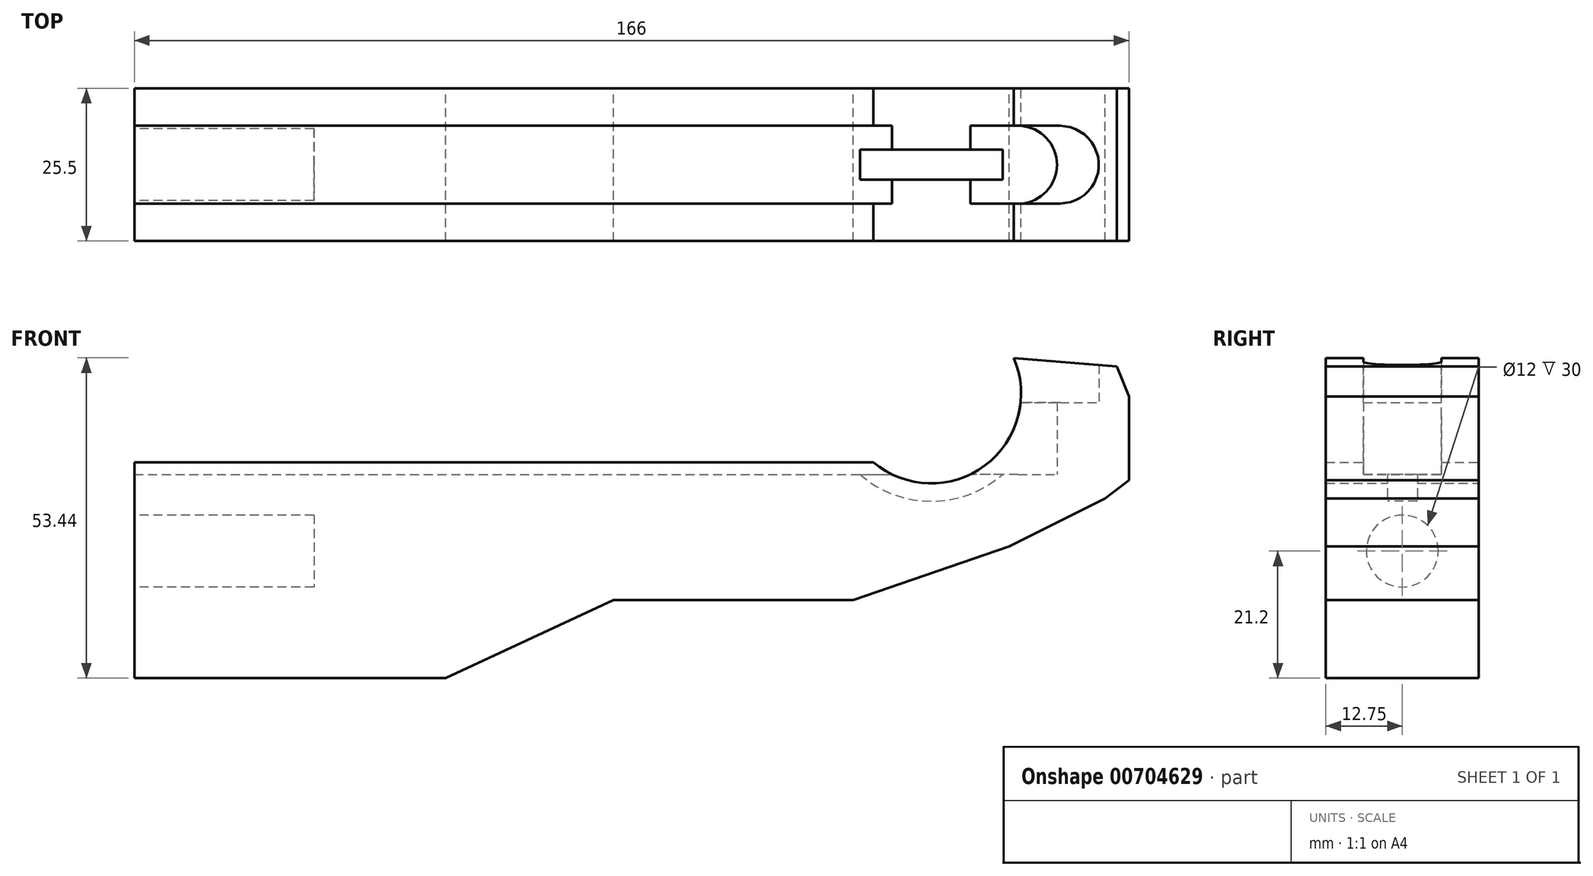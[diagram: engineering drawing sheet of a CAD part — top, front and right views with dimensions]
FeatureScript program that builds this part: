
annotation { "Feature Type Name" : "Feature", "Feature Type Description" : "" }
export const myFeature = defineFeature(function(context is Context, id is Id, definition is map)
    precondition{}
    {
        {
            var Q0;
            Q0=qCreatedBy(makeId("Front.planeOp"),FACE);
            var sketch = newSketch(context, id + "F0", { "sketchPlane" : qUnion([Q0])});
            skLineSegment(sketch, "E0", {"start": v(0, 0) * mm, "end": v(0, 36) * mm});
            skLineSegment(sketch, "E1", {"start": v(0, 36) * mm, "end": v(146, 36) * mm});
            skLineSegment(sketch, "E2", {"start": v(146, 36) * mm, "end": v(146, 53.5) * mm});
            skLineSegment(sketch, "E3", {"start": v(146, 53.5) * mm, "end": v(164, 52) * mm});
            skLineSegment(sketch, "E4", {"start": v(164, 52) * mm, "end": v(166, 47) * mm});
            skLineSegment(sketch, "E5", {"start": v(166, 47) * mm, "end": v(166, 33) * mm});
            skLineSegment(sketch, "E6", {"start": v(166, 33) * mm, "end": v(162, 30) * mm});
            skLineSegment(sketch, "E7", {"start": v(162, 30) * mm, "end": v(146, 22) * mm});
            skLineSegment(sketch, "E8", {"start": v(146, 22) * mm, "end": v(120, 13) * mm});
            skLineSegment(sketch, "E9", {"start": v(120, 13) * mm, "end": v(80, 13) * mm});
            skLineSegment(sketch, "E10", {"start": v(80, 13) * mm, "end": v(52, 0) * mm});
            skLineSegment(sketch, "E11", {"start": v(52, 0) * mm, "end": v(0, 0) * mm});
            skCircle(sketch, "E12", {"center": v(133, 47.5) * mm, "radius": 15 * mm});
            skSolve(sketch);
        }
        {
            var Q0;
            {var subQ4=sQuery(id+"F0.wireOp",EDGE,"E0");Q0=makeQuery(id+"F0.imprint","IMPRINT",FACE,{"disambiguationData":[TD([[makeQuery(id+"F0.imprint","IMPRINT",EDGE,{"derivedFrom":subQ4}),-1.0]])]});}
            var Q1;
            {var subQ0=sQuery(id+"F0.wireOp",EDGE,"E2");var subQ1=sQuery(id+"F0.wireOp",EDGE,"E1");var subQ2=makeQuery(id+"F0.imprint","INTERSECT",VERTEX,{"derivedFrom":[subQ1,subQ0]});Q1=makeQuery(id+"F0.imprint","IMPRINT",FACE,{"disambiguationData":[TD([[makeQuery(id+"F0.imprint","IMPRINT",EDGE,{"disambiguationData":[TD([[subQ2,1.0]])],"derivedFrom":subQ1}),1.0]])]});}
            extrude(context, id + "F1", {"entities" : qUnion([Q0, Q1]), "endBound" : BoundingType.SYMMETRIC, "depth" : 25.5 * mm, "offsetDistance" : 25 * mm});
        }
        {
            var Q0;
            Q0=qCreatedBy(makeId("Front.planeOp"),FACE);
            var sketch = newSketch(context, id + "F2", { "sketchPlane" : qUnion([Q0])});
            skLineSegment(sketch, "E13.0", {"start": v(0, 36) * mm, "end": v(123.37, 36) * mm});
            skArc(sketch, "E14.0", {"start": v(119.15, 36) * mm, "mid": v(141.73, 31.76) * mm, "end": v(150.09, 53.16) * mm});
            skLineSegment(sketch, "E15", {"start": v(0, 34) * mm, "end": v(121.1, 34) * mm});
            skLineSegment(sketch, "E16", {"start": v(0, 36) * mm, "end": v(0, 34) * mm});
            skArc(sketch, "E17.0", {"start": v(123.37, 36) * mm, "mid": v(141.96, 35.47) * mm, "end": v(146.78, 53.44) * mm});
            skLineSegment(sketch, "E18.0", {"start": v(146.78, 53.44) * mm, "end": v(150.09, 53.16) * mm});
            skPoint(sketch, "E19.orphan", {"position": v(164, 52) * mm});
            skSolve(sketch);
        }
        {
            var Q0;
            {var subQ5=sQuery(id+"F2.wireOp",EDGE,"E17.0");Q0=makeQuery(id+"F2.imprint","IMPRINT",FACE,{"disambiguationData":[TD([[makeQuery(id+"F2.imprint","IMPRINT",EDGE,{"derivedFrom":subQ5}),-1.0]])]});}
            extrude(context, id + "F3", {"entities" : qUnion([Q0]), "operationType" : NewBodyOperationType.REMOVE, "endBound" : BoundingType.SYMMETRIC, "oppositeDirection" : true, "depth" : 5 * mm, "offsetDistance" : 25 * mm});
        }
        {
            var Q0;
            Q0=qCreatedBy(makeId("Front.planeOp"),FACE);
            var sketch = newSketch(context, id + "F4", { "sketchPlane" : qUnion([Q0])});
            skLineSegment(sketch, "E20.0", {"start": v(0, 36) * mm, "end": v(119.15, 36) * mm});
            skLineSegment(sketch, "E21.0", {"start": v(0, 34) * mm, "end": v(121.1, 34) * mm});
            skLineSegment(sketch, "E22.0", {"start": v(0, 36) * mm, "end": v(0, 34) * mm});
            skPoint(sketch, "E23.orphan", {"position": v(150.09, 53.16) * mm});
            skPoint(sketch, "E24.orphan", {"position": v(123.37, 36) * mm});
            skLineSegment(sketch, "E25", {"start": v(121.1, 34) * mm, "end": v(129.15, 34) * mm});
            skLineSegment(sketch, "E26", {"start": v(129.15, 34) * mm, "end": v(129.15, 36) * mm});
            skLineSegment(sketch, "E27", {"start": v(119.15, 36) * mm, "end": v(129.15, 36) * mm});
            skSolve(sketch);
        }
        {
            var Q0;
            Q0 = qSketchRegion(id + "F4", true);
            extrude(context, id + "F5", {"entities" : qUnion([Q0]), "operationType" : NewBodyOperationType.REMOVE, "endBound" : BoundingType.SYMMETRIC, "oppositeDirection" : true, "depth" : 13 * mm, "offsetDistance" : 25 * mm});
        }
        {
            var Q0;
            Q0=makeQuery(id+"F5.boolean.opBoolean","COPY",FACE,{"derivedFrom":makeQuery(id+"F5.opExtrude","SWEPT_FACE",FACE,{"disambiguationData":[OSD([sQuery(id+"F4.wireOp",EDGE,"E21.0"),sQuery(id+"F4.wireOp",EDGE,"E25")])]})});
            var sketch = newSketch(context, id + "F6", { "sketchPlane" : qUnion([Q0])});
            skCircle(sketch, "E28", {"center": v(147.5, 0) * mm, "radius": 6.5 * mm});
            skLineSegment(sketch, "E29.bottom", {"start": v(147.5, 6.5) * mm, "end": v(132.5, 6.5) * mm});
            skLineSegment(sketch, "E29.top", {"start": v(147.5, -6.5) * mm, "end": v(132.5, -6.5) * mm});
            skLineSegment(sketch, "E29.left", {"start": v(147.5, 6.5) * mm, "end": v(147.5, -6.5) * mm});
            skLineSegment(sketch, "E29.right", {"start": v(132.5, 6.5) * mm, "end": v(132.5, -6.5) * mm});
            skSolve(sketch);
        }
        {
            var Q0;
            Q0 = qSketchRegion(id + "F6", true);
            extrude(context, id + "F7", {"entities" : qUnion([Q0]), "operationType" : NewBodyOperationType.REMOVE, "depth" : 40.9 * mm, "offsetDistance" : 25 * mm});
        }
        {
            var Q0;
            Q0=makeQuery(id+"F7.boolean.opBoolean","COPY",FACE,{"derivedFrom":makeQuery(id+"F7.opExtrude","CAP_FACE",FACE,{"disambiguationData":[OSD([sQuery(id+"F6.wireOp",EDGE,"E28"),sQuery(id+"F6.wireOp",EDGE,"E29.bottom"),sQuery(id+"F6.wireOp",EDGE,"E29.top"),sQuery(id+"F6.wireOp",EDGE,"E29.right")])],"isStart":true})});
            cPlane(context, id + "F8", {"entities" : qUnion([Q0]), "cplaneType" : CPlaneType.OFFSET, "offset" : 12 * mm, "width" : 150 * mm, "height" : 150 * mm});
        }
        {
            var Q0;
            Q0=qCreatedBy(id+"F8.planeOp",FACE);
            var sketch = newSketch(context, id + "F9", { "sketchPlane" : qUnion([Q0])});
            skCircle(sketch, "E30", {"center": v(154.5, 0) * mm, "radius": 6.5 * mm});
            skLineSegment(sketch, "E31.bottom", {"start": v(154.5, 6.5) * mm, "end": v(139.5, 6.5) * mm});
            skLineSegment(sketch, "E31.top", {"start": v(154.5, -6.5) * mm, "end": v(139.5, -6.5) * mm});
            skLineSegment(sketch, "E31.left", {"start": v(154.5, 6.5) * mm, "end": v(154.5, -6.5) * mm});
            skLineSegment(sketch, "E31.right", {"start": v(139.5, 6.5) * mm, "end": v(139.5, -6.5) * mm});
            skSolve(sketch);
        }
        {
            var Q0;
            Q0 = qSketchRegion(id + "F9", true);
            extrude(context, id + "F10", {"entities" : qUnion([Q0]), "operationType" : NewBodyOperationType.REMOVE, "depth" : 27.7 * mm, "offsetDistance" : 25 * mm});
        }
        {
            var Q0;
            Q0=makeQuery(id+"F1.opExtrude","SWEPT_FACE",FACE,{"disambiguationData":[OSD([sQuery(id+"F0.wireOp",EDGE,"E0")])]});
            var sketch = newSketch(context, id + "F11", { "sketchPlane" : qUnion([Q0])});
            skCircle(sketch, "E32", {"center": v(0, 21.2) * mm, "radius": 6 * mm});
            skCircle(sketch, "E33", {"center": v(0, 21.2) * mm, "radius": 4.9 * mm});
            skSolve(sketch);
        }
        {
            var Q0;
            Q0 = qSketchRegion(id + "F11", true);
            var Q1;
            Q1=makeQuery(id+"F11.imprint","IMPRINT",FACE,{"disambiguationData":[TD([[makeQuery(id+"F11.imprint","IMPRINT",EDGE,{"derivedFrom":sQuery(id+"F11.wireOp",EDGE,"E33")}),1.0]])]});
            extrude(context, id + "F12", {"entities" : qUnion([Q0, Q1]), "operationType" : NewBodyOperationType.REMOVE, "oppositeDirection" : true, "depth" : 30 * mm, "offsetDistance" : 25 * mm});
        }
    });
